# Revit family: Building-ConnessioniIEC309-GEWISS-67IB-PRESE-INTERBLOCCATE_IP67_SENZA_FONDO_63A
name_source: partatom
category: Apparecchi elettrici
units: mm (PartAtom-declared; Revit-internal decimal feet)

## family parameters
Condiviso = Sì
Host = Superficie
Mantenere orientamento annotazione = Sì
Punto di calcolo locali = Sì
Quota connettore circolare = Usa diametro
Taglio con vuoti quando caricato = Sì
Tipo di parte = Normale

## types (11) — shared parameters
Catalogo = BUILDING
Catalogo Serie = 67 IB
Codice Electrocod = 2222
Con fondo = No
Corpo presa = GEWISS -BLU
Corrente nominale (A) = 63
Corrente nominale (In) = 63
Frequenza = 50/60 Hz
Frequenza nominale (Hz) = 50/60 Hz
Glow Wire Test = 850 °C
Glow wire test: = 850 °C
Grado di protezione = IP67
IDF = a2023e9e-4004-42b4-8b9e-55e5b3e28333
IDT = 3210f2e1-5490-4980-ba84-a365430e0752
Immagine tipo = D.jpg
Produttore = GEWISS S.p.A.
Prospetto di default = 1219 mm
Protezione = NO (SBF)
Resistenza agli urti = IK08
SEO = Presa
Scheda Tecnica = https://www.gewiss.com
Simbolo presa = PRESAINDSTAGNA : 3P
Struttura = Grigio RAL - 7035
Temperatura di funzionamento = -25 ÷ +40 °C
Temperatura di utilizzo = -25 +40 °C
Termopressione con biglia = 125 °C
Tipologia = Verticale
URL = https://www.gewiss.com
Versione file RFA = 21.4
presa = Giallo
zero-valued in all types: giallo

## per-type parameters (varying)
| type | Codice EAN | Colore | Colore: | Descrizione | Modello | N. poli | Numero di poli | Riferimento h | Tensione nominale | Tensione nominale: |
| GW67363N - PR.BL IP67 S.F.3P+T 63A 400V 6H SBF | 8011564742444 | Rosso | Rosso | PR.BL IP67 S.F.3P+T 63A 400V 6H SBF | GW67363N | 3P+T | 3P+T | 6 | 380 - 415 V | 380 - 415 V |
| GW67358N - PR.BL IP67 S.F.3P+N+T 63A 110V 4H SBF | 8011564742390 | Giallo | Giallo | PR.BL IP67 S.F.3P+N+T 63A 110V 4H SBF | GW67358N | 3P+N+T | 3P+N+T | 4 | 100 - 130 V | 100 - 130 V |
| GW67364N - PR.BL IP67 S.F.3P+N+T 63A 400V 6H SBF | 8011564742451 | Rosso | Rosso | PR.BL IP67 S.F.3P+N+T 63A 400V 6H SBF | GW67364N | 3P+N+T | 3P+N+T | 6 | 380 - 415 V | 380 - 415 V |
| GW67356N - PR.BL IP67 S.F.2P+T 63A 110V 4H SBF | 8011564742376 | Giallo | Giallo | PR.BL IP67 S.F.2P+T 63A 110V 4H SBF | GW67356N | 2P+T | 2P+T | 4 | 100 - 130 V | 100 - 130 V |
| GW67357N - PR.BL IP67 S.F.3P+T 63A 110V 4H SBF | 8011564742383 | Giallo | Giallo | PR.BL IP67 S.F.3P+T 63A 110V 4H SBF | GW67357N | 3P+T | 3P+T | 4 | 100 - 130 V | 100 - 130 V |
| GW67361N - PR.BL IP67 S.F.3P+N+T 63A 230V 9H SBF | 8011564742420 | Blu | Blu | PR.BL IP67 S.F.3P+N+T 63A 230V 9H SBF | GW67361N | 3P+N+T | 3P+N+T | 9 | 200 - 250 V | 200 - 250 V |
| GW67359N - PR.BL IP67 S.F.2P+T 63A 230V 6H SBF | 8011564742406 | Blu | Blu | PR.BL IP67 S.F.2P+T 63A 230V 6H SBF | GW67359N | 2P+T | 2P+T | 6 | 200 - 250 V | 200 - 250 V |
| GW67362N - PR.BL IP67 S.F.2P+T 63A 400V 9H SBF | 8011564742437 | Rosso | Rosso | PR.BL IP67 S.F.2P+T 63A 400V 9H SBF | GW67362N | 2P+T | 2P+T | 9 | 380 - 415 V | 380 - 415 V |
| GW67360N - PR.BL IP67 S.F.3P+T 63A 230V 9H SBF | 8011564742413 | Blu | Blu | PR.BL IP67 S.F.3P+T 63A 230V 9H SBF | GW67360N | 3P+T | 3P+T | 9 | 200 - 250 V | 200 - 250 V |
| GW67365N - PR.BL IP67 S.F.3P+T 63A 500V 7H SBF | 8011564742468 | Nero | Nero | PR.BL IP67 S.F.3P+T 63A 500V 7H SBF | GW67365N | 3P+T | 3P+T | 7 | 480 - 500 V | 480 - 500 V |
| GW67366N - PR.BL IP67 S.F.3P+N+T 63A 500V 7H SBF | 8011564742475 | Nero | Nero | PR.BL IP67 S.F.3P+N+T 63A 500V 7H SBF | GW67366N | 3P+N+T | 3P+N+T | 7 | 480 - 500 V | 480 - 500 V |

## geometry (parser evidence)
native form markers: Sweep x7
no freeform markers — native parametric forms only
